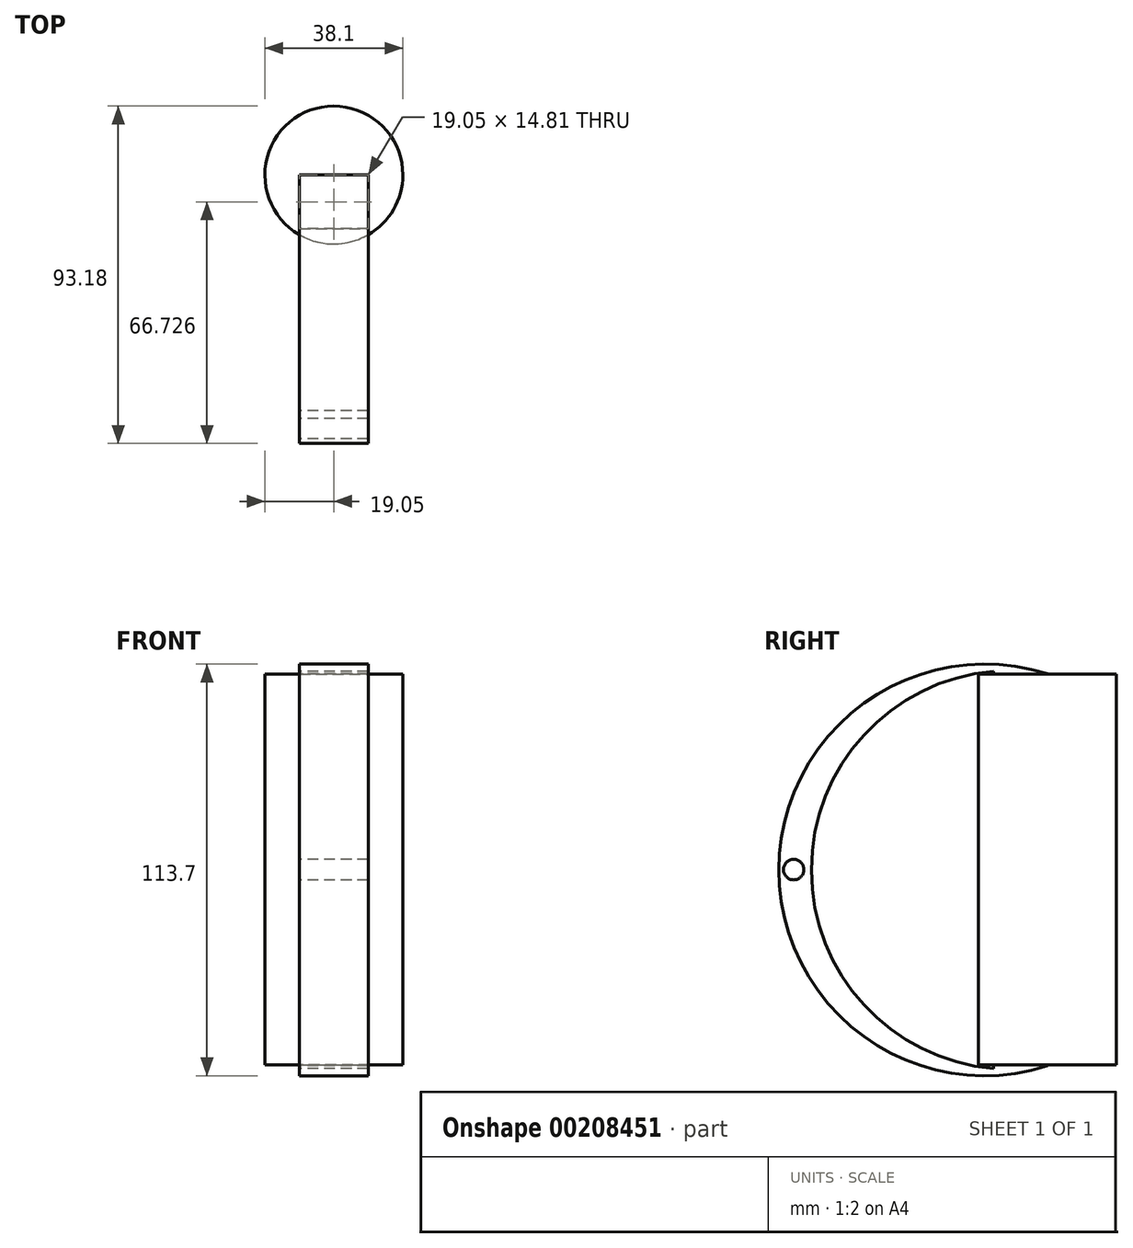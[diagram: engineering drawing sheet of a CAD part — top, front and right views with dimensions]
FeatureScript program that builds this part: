
annotation { "Feature Type Name" : "Feature", "Feature Type Description" : "" }
export const myFeature = defineFeature(function(context is Context, id is Id, definition is map)
    precondition{}
    {
        {
            var Q0;
            Q0=qCreatedBy(makeId("Top.planeOp"),FACE);
            var sketch = newSketch(context, id + "F0", { "sketchPlane" : qUnion([Q0])});
            skCircle(sketch, "E0", {"center": v(0, 0) * mm, "radius": 19.05 * mm});
            skSolve(sketch);
        }
        {
            var Q0;
            Q0=qSketchRegion(id+"F0",true);
            extrude(context, id + "F1", {"entities" : qUnion([Q0]), "endBound" : BoundingType.SYMMETRIC, "depth" : 107.95 * mm});
        }
        {
            var Q0;
            Q0=qCreatedBy(makeId("Right.planeOp"),FACE);
            var sketch = newSketch(context, id + "F2", { "sketchPlane" : qUnion([Q0])});
            skArc(sketch, "E1", {"start": v(0, 54.08) * mm, "mid": v(-74.13, -0.09) * mm, "end": v(0, -54.25) * mm});
            skArc(sketch, "E2", {"start": v(-14.8, 54.8) * mm, "mid": v(-65.17, -0.09) * mm, "end": v(-14.8, -54.98) * mm});
            skCircle(sketch, "E3", {"center": v(-70.06, 0) * mm, "radius": 2.83 * mm});
            skLineSegment(sketch, "E4.left", {"start": v(0, 54.08) * mm, "end": v(0, -54.25) * mm});
            skLineSegment(sketch, "E4.right", {"start": v(-14.8, 54.08) * mm, "end": v(-14.8, -54.25) * mm});
            skLineSegment(sketch, "E5", {"start": v(-14.8, 54.08) * mm, "end": v(-14.8, 54.8) * mm});
            skLineSegment(sketch, "E6", {"start": v(-14.8, -54.25) * mm, "end": v(-14.8, -54.98) * mm});
            skSolve(sketch);
        }
        {
            var Q0;
            Q0=qSketchRegion(id+"F2",true);
            extrude(context, id + "F3", {"entities" : qUnion([Q0]), "operationType" : NewBodyOperationType.ADD, "endBound" : BoundingType.SYMMETRIC, "depth" : 19.05 * mm});
        }
    });
